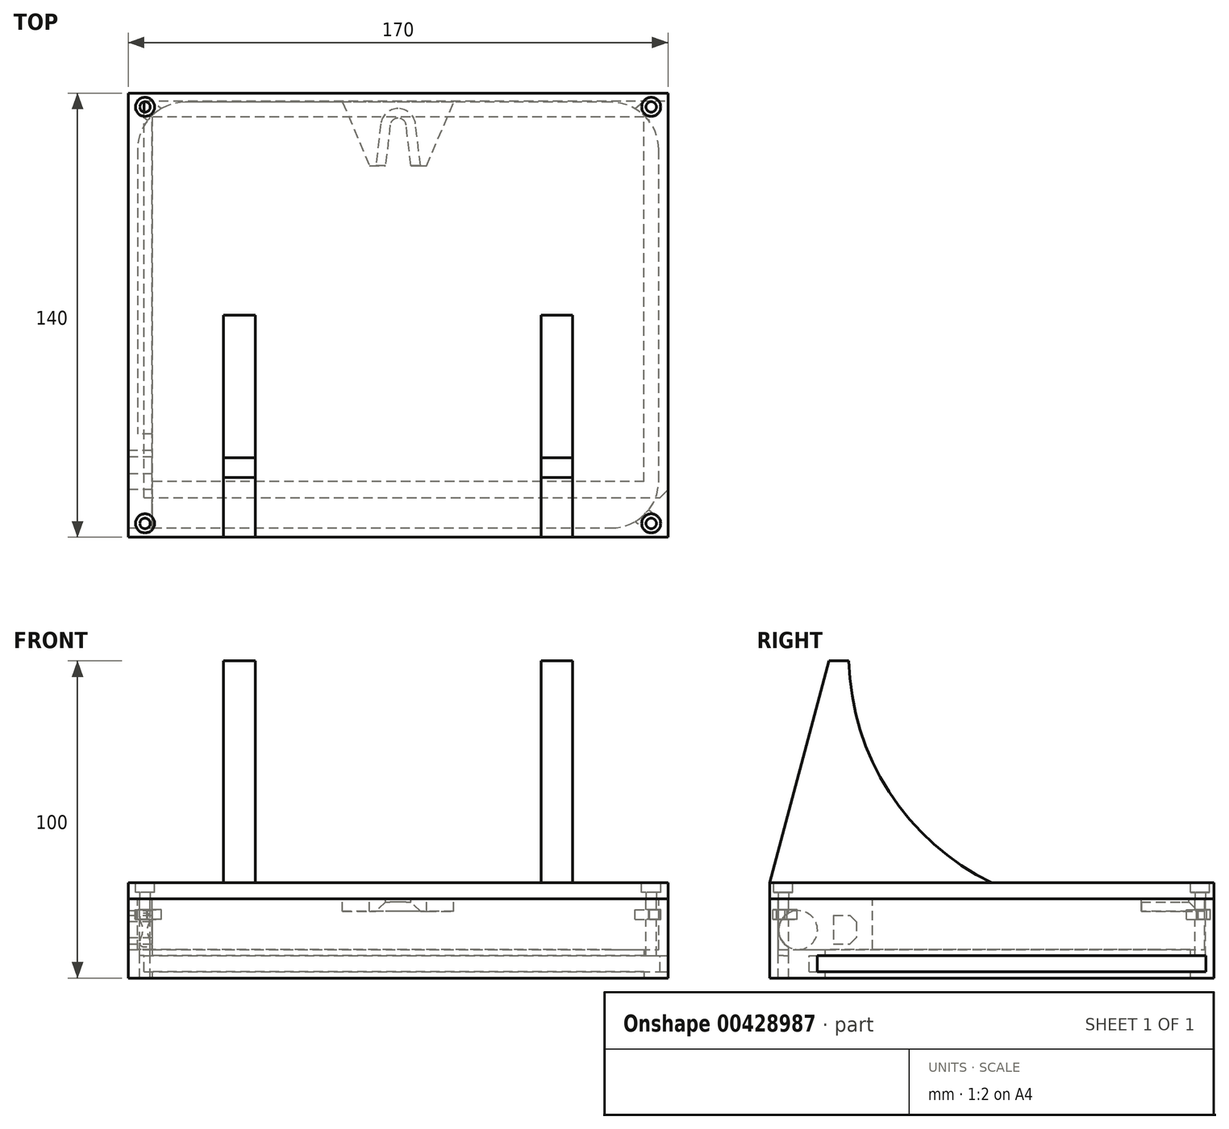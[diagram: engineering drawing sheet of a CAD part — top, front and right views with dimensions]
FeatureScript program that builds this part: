
annotation { "Feature Type Name" : "Feature", "Feature Type Description" : "" }
export const myFeature = defineFeature(function(context is Context, id is Id, definition is map)
    precondition{}
    {
        {
            var Q0;
            Q0=qCreatedBy(makeId("Top.planeOp"),FACE);
            var sketch = newSketch(context, id + "F0", { "sketchPlane" : qUnion([Q0])});
            skLineSegment(sketch, "E0.bottom", {"start": v(0, 0) * mm, "end": v(170, 0) * mm});
            skLineSegment(sketch, "E0.top", {"start": v(0, 140) * mm, "end": v(170, 140) * mm});
            skLineSegment(sketch, "E0.left", {"start": v(0, 0) * mm, "end": v(0, 140) * mm});
            skLineSegment(sketch, "E0.right", {"start": v(170, 0) * mm, "end": v(170, 140) * mm});
            skLineSegment(sketch, "E1.bottom", {"start": v(7.5, 132.5) * mm, "end": v(162.5, 132.5) * mm});
            skLineSegment(sketch, "E1.top", {"start": v(7.5, 17.5) * mm, "end": v(162.5, 17.5) * mm});
            skLineSegment(sketch, "E1.left", {"start": v(7.5, 132.5) * mm, "end": v(7.5, 17.5) * mm});
            skLineSegment(sketch, "E1.right", {"start": v(162.5, 132.5) * mm, "end": v(162.5, 17.5) * mm});
            skSolve(sketch);
        }
        {
            var Q0;
            Q0=qSketchRegion(id+"F0",true);
            extrude(context, id + "F1", {"entities" : qUnion([Q0]), "depth" : 25 * mm});
        }
        {
            var Q0;
            Q0=makeQuery(id+"F1.opExtrude","SWEPT_FACE",FACE,{"disambiguationData":[OSD([sQuery(id+"F0.wireOp",EDGE,"E0.right")])]});
            var sketch = newSketch(context, id + "F2", { "sketchPlane" : qUnion([Q0])});
            skLineSegment(sketch, "E2.0.0", {"start": v(17.5, 0) * mm, "end": v(132.5, 0) * mm, "construction": true});
            skLineSegment(sketch, "E2.0.1", {"start": v(132.5, 0) * mm, "end": v(132.5, 25) * mm, "construction": true});
            skLineSegment(sketch, "E2.0.2", {"start": v(132.5, 25) * mm, "end": v(17.5, 25) * mm, "construction": true});
            skLineSegment(sketch, "E2.0.3", {"start": v(17.5, 25) * mm, "end": v(17.5, 0) * mm, "construction": true});
            skLineSegment(sketch, "E3.0.3", {"start": v(132.5, 25) * mm, "end": v(132.5, 0) * mm, "construction": true});
            skLineSegment(sketch, "E4.bottom", {"start": v(12.5, 2) * mm, "end": v(137.5, 2) * mm});
            skLineSegment(sketch, "E4.top", {"start": v(12.5, 7) * mm, "end": v(137.5, 7) * mm});
            skLineSegment(sketch, "E4.left", {"start": v(12.5, 2) * mm, "end": v(12.5, 7) * mm});
            skLineSegment(sketch, "E4.right", {"start": v(137.5, 2) * mm, "end": v(137.5, 7) * mm});
            skSolve(sketch);
        }
        {
            var Q0;
            Q0=qSketchRegion(id+"F2",true);
            extrude(context, id + "F3", {"entities" : qUnion([Q0]), "operationType" : NewBodyOperationType.REMOVE, "oppositeDirection" : true, "depth" : 165 * mm});
        }
        {
            var Q0;
            Q0=makeQuery(id+"F3.boolean.opBoolean","COPY",FACE,{"derivedFrom":makeQuery(id+"F3.opExtrude","SWEPT_FACE",FACE,{"disambiguationData":[OSD([sQuery(id+"F2.wireOp",EDGE,"E4.top")])]})});
            var sketch = newSketch(context, id + "F4", { "sketchPlane" : qUnion([Q0])});
            skLineSegment(sketch, "E5", {"start": v(167.5, -12.5) * mm, "end": v(170, -15) * mm});
            skLineSegment(sketch, "E6", {"start": v(170, -15) * mm, "end": v(170, -12.5) * mm});
            skLineSegment(sketch, "E7", {"start": v(170, -12.5) * mm, "end": v(167.5, -12.5) * mm});
            skSolve(sketch);
        }
        {
            var Q0;
            Q0=makeQuery(id+"F4.imprint","IMPRINT",FACE,{"disambiguationData":[TD([[makeQuery(id+"F4.imprint","IMPRINT",EDGE,{"derivedFrom":sQuery(id+"F4.wireOp",EDGE,"E5")}),1.0]])]});
            extrude(context, id + "F5", {"entities" : qUnion([Q0]), "operationType" : NewBodyOperationType.ADD, "endBound" : BoundingType.UP_TO_NEXT, "depth" : 25 * mm});
        }
        {
            var Q0;
            Q0=makeQuery(id+"F1.opExtrude","CAP_FACE",FACE,{"disambiguationData":[OSD([sQuery(id+"F0.wireOp",EDGE,"E0.bottom"),sQuery(id+"F0.wireOp",EDGE,"E0.top"),sQuery(id+"F0.wireOp",EDGE,"E0.left"),sQuery(id+"F0.wireOp",EDGE,"E0.right"),sQuery(id+"F0.wireOp",EDGE,"E1.bottom"),sQuery(id+"F0.wireOp",EDGE,"E1.top"),sQuery(id+"F0.wireOp",EDGE,"E1.left"),sQuery(id+"F0.wireOp",EDGE,"E1.right")])],"isStart":false});
            var sketch = newSketch(context, id + "F6", { "sketchPlane" : qUnion([Q0])});
            skLineSegment(sketch, "E8.0", {"start": v(167.12, 137.12) * mm, "end": v(2.88, 137.12) * mm});
            skLineSegment(sketch, "E8.1", {"start": v(167.12, 2.88) * mm, "end": v(167.12, 137.12) * mm});
            skLineSegment(sketch, "E8.2", {"start": v(2.88, 2.88) * mm, "end": v(167.12, 2.88) * mm});
            skLineSegment(sketch, "E8.3", {"start": v(2.88, 137.12) * mm, "end": v(2.88, 2.88) * mm});
            skSolve(sketch);
        }
        {
            var Q0;
            Q0=qSketchRegion(id+"F6",true);
            extrude(context, id + "F7", {"entities" : qUnion([Q0]), "operationType" : NewBodyOperationType.REMOVE, "oppositeDirection" : true, "depth" : 16 * mm});
        }
        {
            var Q0;
            Q0=makeQuery(id+"F7.boolean.opBoolean","COPY",EDGE,{"derivedFrom":makeQuery(id+"F7.opExtrude","SWEPT_EDGE",EDGE,{"disambiguationData":[OSD([sQuery(id+"F6.wireOp",EDGE,"E8.0"),sQuery(id+"F6.wireOp",EDGE,"E8.3")])]})});
            var Q1;
            Q1=makeQuery(id+"F7.boolean.opBoolean","COPY",EDGE,{"derivedFrom":makeQuery(id+"F7.opExtrude","SWEPT_EDGE",EDGE,{"disambiguationData":[OSD([sQuery(id+"F6.wireOp",EDGE,"E8.0"),sQuery(id+"F6.wireOp",EDGE,"E8.1")])]})});
            var Q2;
            Q2=makeQuery(id+"F7.boolean.opBoolean","COPY",EDGE,{"derivedFrom":makeQuery(id+"F7.opExtrude","SWEPT_EDGE",EDGE,{"disambiguationData":[OSD([sQuery(id+"F6.wireOp",EDGE,"E8.1"),sQuery(id+"F6.wireOp",EDGE,"E8.2")])]})});
            fillet(context, id + "F8", {"entities" : qUnion([Q0, Q1, Q2]), "radius" : 15 * mm, "tangentPropagation" : true, "allowEdgeOverflow" : false});
        }
        {
            var Q0;
            Q0=makeQuery(id+"F7.boolean.opBoolean","COPY",FACE,{"derivedFrom":makeQuery(id+"F7.opExtrude","SWEPT_FACE",FACE,{"disambiguationData":[OSD([sQuery(id+"F6.wireOp",EDGE,"E8.3")])]})});
            var sketch = newSketch(context, id + "F9", { "sketchPlane" : qUnion([Q0])});
            skLineSegment(sketch, "E9.0.0", {"start": v(2.88, 9) * mm, "end": v(122.12, 9) * mm, "construction": true});
            skLineSegment(sketch, "E9.0.1", {"start": v(122.12, 9) * mm, "end": v(122.12, 25) * mm, "construction": true});
            skLineSegment(sketch, "E9.0.2", {"start": v(122.12, 25) * mm, "end": v(2.88, 25) * mm, "construction": true});
            skLineSegment(sketch, "E9.0.3", {"start": v(2.88, 25) * mm, "end": v(2.88, 9) * mm, "construction": true});
            skCircle(sketch, "E10", {"center": v(9, 15.13) * mm, "radius": 6.12 * mm});
            skSolve(sketch);
        }
        {
            var Q0;
            {var subQ0=sQuery(id+"F9.wireOp",EDGE,"E10");var subQ1=sQuery(id+"F6.wireOp",EDGE,"E8.3");var subQ3=makeQuery(id+"F9.imprint","INTERSECT",VERTEX,{"derivedFrom":[makeQuery(id+"F7.boolean.opBoolean","COPY",EDGE,{"derivedFrom":makeQuery(id+"F7.opExtrude","CAP_EDGE",EDGE,{"disambiguationData":[OSD([subQ1])],"isStart":false})}),subQ0]});Q0=makeQuery(id+"F9.imprint","IMPRINT",FACE,{"disambiguationData":[TD([[makeQuery(id+"F9.imprint","IMPRINT",EDGE,{"disambiguationData":[TD([[subQ3,1.0]])],"derivedFrom":subQ0}),1.0]])]});}
            extrude(context, id + "F10", {"entities" : qUnion([Q0]), "operationType" : NewBodyOperationType.REMOVE, "endBound" : BoundingType.THROUGH_ALL, "oppositeDirection" : true, "depth" : 25 * mm});
        }
        {
            var Q0;
            {var subQ0=sQuery(id+"F6.wireOp",EDGE,"E8.3");var subQ1=makeQuery(id+"F7.boolean.opBoolean","COPY",FACE,{"derivedFrom":makeQuery(id+"F7.opExtrude","SWEPT_FACE",FACE,{"disambiguationData":[OSD([subQ0])]})});var subQ2=sQuery(id+"F6.wireOp",EDGE,"E8.2");var subQ3=sQuery(id+"F6.wireOp",EDGE,"E8.0");Q0=makeQuery(id+"F10.boolean.opBoolean","SPLIT",FACE,{"disambiguationData":[TD([makeQuery(id+"F1.opExtrude","CAP_FACE",FACE,{"disambiguationData":[OSD([sQuery(id+"F0.wireOp",EDGE,"E0.bottom"),sQuery(id+"F0.wireOp",EDGE,"E0.top"),sQuery(id+"F0.wireOp",EDGE,"E0.left"),sQuery(id+"F0.wireOp",EDGE,"E0.right"),sQuery(id+"F0.wireOp",EDGE,"E1.bottom"),sQuery(id+"F0.wireOp",EDGE,"E1.top"),sQuery(id+"F0.wireOp",EDGE,"E1.left"),sQuery(id+"F0.wireOp",EDGE,"E1.right")])],"isStart":false}),makeQuery(id+"F7.boolean.opBoolean","COPY",FACE,{"derivedFrom":makeQuery(id+"F7.opExtrude","CAP_FACE",FACE,{"disambiguationData":[OSD([subQ3,sQuery(id+"F6.wireOp",EDGE,"E8.1"),subQ2,subQ0])],"isStart":false})}),makeQuery(id+"F7.boolean.opBoolean","COPY",FACE,{"derivedFrom":makeQuery(id+"F7.opExtrude","SWEPT_FACE",FACE,{"disambiguationData":[OSD([subQ2])]})}),subQ1,makeQuery(id+"F8.opFillet","BLEND_FACE",FACE,{"disambiguationData":[OSD([subQ3,subQ0])]}),makeQuery(id+"F10.opExtrude","SWEPT_FACE",FACE,{"disambiguationData":[OSD([sQuery(id+"F9.wireOp",EDGE,"E10")])]})])],"derivedFrom":subQ1});}
            var sketch = newSketch(context, id + "F11", { "sketchPlane" : qUnion([Q0])});
            skArc(sketch, "E11.0", {"start": v(9, 9) * mm, "mid": v(13.34, 19.46) * mm, "end": v(2.88, 15.13) * mm});
            skArc(sketch, "E12.0", {"start": v(2.88, 15.13) * mm, "mid": v(4.67, 10.8) * mm, "end": v(9, 9) * mm});
            skLineSegment(sketch, "E13.bottom", {"start": v(2.88, 9) * mm, "end": v(17.5, 9) * mm});
            skLineSegment(sketch, "E13.top", {"start": v(2.88, 25) * mm, "end": v(17.5, 25) * mm});
            skLineSegment(sketch, "E13.left", {"start": v(2.88, 9) * mm, "end": v(2.88, 25) * mm});
            skLineSegment(sketch, "E13.right", {"start": v(17.5, 9) * mm, "end": v(17.5, 9) * mm});
            skLineSegment(sketch, "E14.0", {"start": v(17.5, 9) * mm, "end": v(17.5, 7) * mm, "construction": true});
            skLineSegment(sketch, "E15", {"start": v(17.5, 9) * mm, "end": v(17.5, 25) * mm});
            skSolve(sketch);
        }
        {
            var Q0;
            Q0=qSketchRegion(id+"F11",true);
            var Q1;
            {var subQ0=sQuery(id+"F0.wireOp",EDGE,"E1.left");Q1=makeQuery(id+"F3.boolean.opBoolean","SPLIT",FACE,{"disambiguationData":[TD([makeQuery(id+"F3.opExtrude","SWEPT_FACE",FACE,{"disambiguationData":[OSD([sQuery(id+"F2.wireOp",EDGE,"E4.top")])]})])],"derivedFrom":makeQuery(id+"F1.opExtrude","SWEPT_FACE",FACE,{"disambiguationData":[OSD([subQ0])]})});}
            extrude(context, id + "F12", {"entities" : qUnion([Q0]), "operationType" : NewBodyOperationType.ADD, "endBound" : BoundingType.UP_TO_SURFACE, "endBoundEntityFace" : qUnion([Q1]), "depth" : 7.5 * mm});
        }
        {
            var Q0;
            Q0=makeQuery(id+"F12.opExtrude","CAP_FACE",FACE,{"disambiguationData":[OSD([sQuery(id+"F11.wireOp",EDGE,"E13.bottom"),sQuery(id+"F11.wireOp",EDGE,"E13.top"),sQuery(id+"F11.wireOp",EDGE,"E13.left"),sQuery(id+"F11.wireOp",EDGE,"E15")])],"isStart":true});
            extrude(context, id + "F13", {"entities" : qUnion([Q0]), "operationType" : NewBodyOperationType.REMOVE, "endBound" : BoundingType.UP_TO_NEXT, "oppositeDirection" : true, "depth" : 25 * mm});
        }
        {
            var Q0;
            Q0=makeQuery(id+"F12.opExtrude","SWEPT_FACE",FACE,{"disambiguationData":[OSD([sQuery(id+"F11.wireOp",EDGE,"E15")])]});
            extrude(context, id + "F14", {"entities" : qUnion([Q0]), "operationType" : NewBodyOperationType.ADD, "depth" : 15 * mm});
        }
        {
            var Q0;
            {var subQ0=sQuery(id+"F11.wireOp",EDGE,"E15");var subQ1=sQuery(id+"F6.wireOp",EDGE,"E8.2");var subQ2=sQuery(id+"F11.wireOp",EDGE,"E13.top");var subQ3=makeQuery(id+"F12.opExtrude","CAP_FACE",FACE,{"disambiguationData":[OSD([sQuery(id+"F11.wireOp",EDGE,"E13.bottom"),subQ2,sQuery(id+"F11.wireOp",EDGE,"E13.left"),subQ0])],"isStart":false});var subQ4=sQuery(id+"F0.wireOp",EDGE,"E1.left");var subQ5=makeQuery(id+"F1.opExtrude","SWEPT_FACE",FACE,{"disambiguationData":[OSD([subQ4])]});var subQ6=sQuery(id+"F0.wireOp",EDGE,"E1.top");var subQ7=makeQuery(id+"F1.opExtrude","SWEPT_FACE",FACE,{"disambiguationData":[OSD([subQ6])]});var subQ8=sQuery(id+"F0.wireOp",EDGE,"E1.bottom");var subQ9=makeQuery(id+"F1.opExtrude","CAP_FACE",FACE,{"disambiguationData":[OSD([sQuery(id+"F0.wireOp",EDGE,"E0.bottom"),sQuery(id+"F0.wireOp",EDGE,"E0.top"),sQuery(id+"F0.wireOp",EDGE,"E0.left"),sQuery(id+"F0.wireOp",EDGE,"E0.right"),subQ8,subQ6,subQ4,sQuery(id+"F0.wireOp",EDGE,"E1.right")])],"isStart":false});var subQ10=sQuery(id+"F9.wireOp",EDGE,"E10");Q0=makeQuery(id+"F14.boolean.opBoolean","MERGE",FACE,{"derivedFrom":[makeQuery(id+"F3.boolean.opBoolean","SPLIT",FACE,{"disambiguationData":[TD([makeQuery(id+"F3.opExtrude","SWEPT_FACE",FACE,{"disambiguationData":[OSD([sQuery(id+"F2.wireOp",EDGE,"E4.top")])]})])],"derivedFrom":subQ5}),makeQuery(id+"F13.boolean.opBoolean","SPLIT",FACE,{"disambiguationData":[TD([subQ9,subQ7,subQ5,makeQuery(id+"F7.boolean.opBoolean","COPY",FACE,{"derivedFrom":makeQuery(id+"F7.opExtrude","CAP_FACE",FACE,{"disambiguationData":[OSD([sQuery(id+"F6.wireOp",EDGE,"E8.0"),sQuery(id+"F6.wireOp",EDGE,"E8.1"),subQ1,sQuery(id+"F6.wireOp",EDGE,"E8.3")])],"isStart":false})}),makeQuery(id+"F7.boolean.opBoolean","COPY",FACE,{"derivedFrom":makeQuery(id+"F7.opExtrude","SWEPT_FACE",FACE,{"disambiguationData":[OSD([subQ1])]})}),makeQuery(id+"F10.boolean.opBoolean","COPY",FACE,{"derivedFrom":makeQuery(id+"F10.opExtrude","SWEPT_FACE",FACE,{"disambiguationData":[OSD([subQ10])]})}),subQ3,makeQuery(id+"F12.opExtrude","SWEPT_FACE",FACE,{"disambiguationData":[OSD([subQ2])]}),makeQuery(id+"F12.opExtrude","SWEPT_FACE",FACE,{"disambiguationData":[OSD([subQ0])]}),makeQuery(id+"F13.opExtrude","SWEPT_FACE",FACE,{"disambiguationData":[OSD([subQ10])]})])],"derivedFrom":subQ3}),makeQuery(id+"F14.opExtrude","SWEPT_FACE",FACE,{"disambiguationData":[OSD([subQ0]),TDD([makeQuery(id+"F12.opExtrude","CAP_EDGE",EDGE,{"disambiguationData":[OSD([subQ0])],"isStart":false})])]})]});}
            var sketch = newSketch(context, id + "F15", { "sketchPlane" : qUnion([Q0])});
            skLineSegment(sketch, "E16.bottom", {"start": v(20.13, 19.75) * mm, "end": v(27.38, 19.75) * mm});
            skLineSegment(sketch, "E16.top", {"start": v(20.13, 10.75) * mm, "end": v(27.38, 10.75) * mm});
            skLineSegment(sketch, "E16.left", {"start": v(20.13, 19.75) * mm, "end": v(20.13, 10.75) * mm});
            skLineSegment(sketch, "E16.right", {"start": v(27.38, 19.75) * mm, "end": v(27.38, 10.75) * mm});
            skLineSegment(sketch, "E17.0", {"start": v(9, 9) * mm, "end": v(17.5, 9) * mm, "construction": true});
            skSolve(sketch);
        }
        {
            var Q0;
            Q0=makeQuery(id+"F15.imprint","IMPRINT",FACE,{"disambiguationData":[TD([[makeQuery(id+"F15.imprint","IMPRINT",EDGE,{"derivedFrom":sQuery(id+"F15.wireOp",EDGE,"E16.bottom")}),-1.0]])]});
            extrude(context, id + "F16", {"entities" : qUnion([Q0]), "operationType" : NewBodyOperationType.REMOVE, "endBound" : BoundingType.UP_TO_NEXT, "oppositeDirection" : true, "depth" : 25 * mm});
        }
        {
            var Q0;
            Q0=makeQuery(id+"F16.boolean.opBoolean","COPY",EDGE,{"derivedFrom":makeQuery(id+"F16.opExtrude","SWEPT_EDGE",EDGE,{"disambiguationData":[OSD([sQuery(id+"F15.wireOp",EDGE,"E16.top"),sQuery(id+"F15.wireOp",EDGE,"E16.right")])]})});
            var Q1;
            Q1=makeQuery(id+"F16.boolean.opBoolean","COPY",EDGE,{"derivedFrom":makeQuery(id+"F16.opExtrude","SWEPT_EDGE",EDGE,{"disambiguationData":[OSD([sQuery(id+"F15.wireOp",EDGE,"E16.bottom"),sQuery(id+"F15.wireOp",EDGE,"E16.right")])]})});
            chamfer(context, id + "F17", {"entities" : qUnion([Q0, Q1]), "width" : 2 * mm, "tangentPropagation" : true});
        }
        {
            var Q0;
            {var subQ0=sQuery(id+"F11.wireOp",EDGE,"E13.top");Q0=makeQuery(id+"F14.boolean.opBoolean","MERGE",FACE,{"derivedFrom":[makeQuery(id+"F12.boolean.opBoolean","MERGE",FACE,{"derivedFrom":[makeQuery(id+"F1.opExtrude","CAP_FACE",FACE,{"disambiguationData":[OSD([sQuery(id+"F0.wireOp",EDGE,"E0.bottom"),sQuery(id+"F0.wireOp",EDGE,"E0.top"),sQuery(id+"F0.wireOp",EDGE,"E0.left"),sQuery(id+"F0.wireOp",EDGE,"E0.right"),sQuery(id+"F0.wireOp",EDGE,"E1.bottom"),sQuery(id+"F0.wireOp",EDGE,"E1.top"),sQuery(id+"F0.wireOp",EDGE,"E1.left"),sQuery(id+"F0.wireOp",EDGE,"E1.right")])],"isStart":false}),makeQuery(id+"F12.opExtrude","SWEPT_FACE",FACE,{"disambiguationData":[OSD([subQ0])]})]}),makeQuery(id+"F14.opExtrude","SWEPT_FACE",FACE,{"disambiguationData":[OSD([sQuery(id+"F6.wireOp",EDGE,"E8.3"),subQ0,sQuery(id+"F11.wireOp",EDGE,"E15")])]})]});}
            var sketch = newSketch(context, id + "F18", { "sketchPlane" : qUnion([Q0])});
            skLineSegment(sketch, "E18", {"start": v(67.5, 137.12) * mm, "end": v(76, 117.12) * mm});
            skLineSegment(sketch, "E19", {"start": v(76, 117.12) * mm, "end": v(81, 117.12) * mm});
            skLineSegment(sketch, "E20", {"start": v(89, 117.12) * mm, "end": v(87.25, 132.12) * mm});
            skLineSegment(sketch, "E21", {"start": v(82.75, 132.12) * mm, "end": v(87.25, 132.12) * mm});
            skLineSegment(sketch, "E22", {"start": v(82.75, 132.12) * mm, "end": v(81, 117.12) * mm});
            skLineSegment(sketch, "E23", {"start": v(89, 117.12) * mm, "end": v(94, 117.12) * mm});
            skLineSegment(sketch, "E24", {"start": v(94, 117.12) * mm, "end": v(102.5, 137.12) * mm});
            skLineSegment(sketch, "E25", {"start": v(102.5, 137.12) * mm, "end": v(67.5, 137.12) * mm});
            skSolve(sketch);
        }
        {
            var Q0;
            Q0=qSketchRegion(id+"F18",true);
            extrude(context, id + "F19", {"entities" : qUnion([Q0]), "operationType" : NewBodyOperationType.ADD, "oppositeDirection" : true, "depth" : 4 * mm});
        }
        {
            var Q0;
            Q0=makeQuery(id+"F19.opExtrude","SWEPT_EDGE",EDGE,{"disambiguationData":[OSD([sQuery(id+"F18.wireOp",EDGE,"E21"),sQuery(id+"F18.wireOp",EDGE,"E22")])]});
            var Q1;
            Q1=makeQuery(id+"F19.opExtrude","SWEPT_EDGE",EDGE,{"disambiguationData":[OSD([sQuery(id+"F18.wireOp",EDGE,"E20"),sQuery(id+"F18.wireOp",EDGE,"E21")])]});
            fillet(context, id + "F20", {"entities" : qUnion([Q0, Q1]), "radius" : 2.5 * mm, "tangentPropagation" : true, "allowEdgeOverflow" : false});
        }
        {
            var Q0;
            {var subQ0=sQuery(id+"F18.wireOp",EDGE,"E22");var subQ1=sQuery(id+"F18.wireOp",EDGE,"E21");Q0=makeQuery(id+"F20.opFillet","BLEND_EDGE",EDGE,{"blendedFrom":[makeQuery(id+"F19.opExtrude","SWEPT_EDGE",EDGE,{"disambiguationData":[OSD([subQ1,subQ0])]}),makeQuery(id+"F19.opExtrude","CAP_FACE",FACE,{"disambiguationData":[OSD([sQuery(id+"F18.wireOp",EDGE,"E18"),sQuery(id+"F18.wireOp",EDGE,"E19"),sQuery(id+"F18.wireOp",EDGE,"E20"),subQ1,subQ0,sQuery(id+"F18.wireOp",EDGE,"E23"),sQuery(id+"F18.wireOp",EDGE,"E24"),sQuery(id+"F18.wireOp",EDGE,"E25")])],"isStart":false})],"blendedInto":[makeQuery(id+"F19.opExtrude","CAP_FACE",FACE,{"disambiguationData":[OSD([sQuery(id+"F18.wireOp",EDGE,"E18"),sQuery(id+"F18.wireOp",EDGE,"E19"),sQuery(id+"F18.wireOp",EDGE,"E20"),subQ1,subQ0,sQuery(id+"F18.wireOp",EDGE,"E23"),sQuery(id+"F18.wireOp",EDGE,"E24"),sQuery(id+"F18.wireOp",EDGE,"E25")])],"isStart":false})]});}
            chamfer(context, id + "F21", {"entities" : qUnion([Q0]), "width" : 3 * mm, "tangentPropagation" : true});
        }
        {
            var Q0;
            {var subQ0=sQuery(id+"F11.wireOp",EDGE,"E13.top");Q0=makeQuery(id+"F19.boolean.opBoolean","MERGE",FACE,{"derivedFrom":[makeQuery(id+"F14.boolean.opBoolean","MERGE",FACE,{"derivedFrom":[makeQuery(id+"F12.boolean.opBoolean","MERGE",FACE,{"derivedFrom":[makeQuery(id+"F1.opExtrude","CAP_FACE",FACE,{"disambiguationData":[OSD([sQuery(id+"F0.wireOp",EDGE,"E0.bottom"),sQuery(id+"F0.wireOp",EDGE,"E0.top"),sQuery(id+"F0.wireOp",EDGE,"E0.left"),sQuery(id+"F0.wireOp",EDGE,"E0.right"),sQuery(id+"F0.wireOp",EDGE,"E1.bottom"),sQuery(id+"F0.wireOp",EDGE,"E1.top"),sQuery(id+"F0.wireOp",EDGE,"E1.left"),sQuery(id+"F0.wireOp",EDGE,"E1.right")])],"isStart":false}),makeQuery(id+"F12.opExtrude","SWEPT_FACE",FACE,{"disambiguationData":[OSD([subQ0])]})]}),makeQuery(id+"F14.opExtrude","SWEPT_FACE",FACE,{"disambiguationData":[OSD([sQuery(id+"F6.wireOp",EDGE,"E8.3"),subQ0,sQuery(id+"F11.wireOp",EDGE,"E15")])]})]}),makeQuery(id+"F19.opExtrude","CAP_FACE",FACE,{"disambiguationData":[OSD([sQuery(id+"F18.wireOp",EDGE,"E18"),sQuery(id+"F18.wireOp",EDGE,"E19"),sQuery(id+"F18.wireOp",EDGE,"E20"),sQuery(id+"F18.wireOp",EDGE,"E21"),sQuery(id+"F18.wireOp",EDGE,"E22"),sQuery(id+"F18.wireOp",EDGE,"E23"),sQuery(id+"F18.wireOp",EDGE,"E24"),sQuery(id+"F18.wireOp",EDGE,"E25")])],"isStart":true})]});}
            cPlane(context, id + "F22", {"entities" : qUnion([Q0]), "cplaneType" : CPlaneType.OFFSET, "offset" : 5 * mm, "oppositeDirection" : true, "width" : 150 * mm, "height" : 150 * mm});
        }
        {
            var Q0;
            Q0=qCreatedBy(id+"F22.planeOp",FACE);
            var sketch = newSketch(context, id + "F23", { "sketchPlane" : qUnion([Q0])});
            skLineSegment(sketch, "E26.0.0", {"start": v(170, 140) * mm, "end": v(0, 140) * mm, "construction": true});
            skLineSegment(sketch, "E26.0.1", {"start": v(0, 140) * mm, "end": v(0, 0) * mm, "construction": true});
            skLineSegment(sketch, "E26.0.2", {"start": v(0, 0) * mm, "end": v(170, 0) * mm, "construction": true});
            skLineSegment(sketch, "E26.0.3", {"start": v(170, 0) * mm, "end": v(170, 140) * mm, "construction": true});
            skLineSegment(sketch, "E27", {"start": v(0, 140) * mm, "end": v(170, 0) * mm, "construction": true});
            skLineSegment(sketch, "E28", {"start": v(0, 0) * mm, "end": v(170, 140) * mm, "construction": true});
            skCircle(sketch, "E29.cCircle", {"center": v(5.27, 135.66) * mm, "radius": 2.85 * mm, "construction": true});
            skLineSegment(sketch, "E29.0", {"start": v(5.81, 138.9) * mm, "end": v(8.35, 136.81) * mm});
            skLineSegment(sketch, "E29.1", {"start": v(8.35, 136.81) * mm, "end": v(7.81, 133.57) * mm, "construction": true});
            skLineSegment(sketch, "E29.2", {"start": v(7.81, 133.57) * mm, "end": v(4.73, 132.41) * mm, "construction": true});
            skLineSegment(sketch, "E29.3", {"start": v(4.73, 132.41) * mm, "end": v(2.2, 134.5) * mm});
            skLineSegment(sketch, "E29.4", {"start": v(2.2, 134.5) * mm, "end": v(2.73, 137.75) * mm});
            skLineSegment(sketch, "E29.5", {"start": v(2.73, 137.75) * mm, "end": v(5.81, 138.9) * mm});
            skPoint(sketch, "E29.0.midPoint", {"position": v(7.08, 137.86) * mm});
            skCircle(sketch, "E30.cCircle", {"center": v(164.73, 135.66) * mm, "radius": 2.85 * mm, "construction": true});
            skLineSegment(sketch, "E30.0", {"start": v(161.65, 136.81) * mm, "end": v(164.19, 138.9) * mm});
            skLineSegment(sketch, "E30.1", {"start": v(164.19, 138.9) * mm, "end": v(167.27, 137.75) * mm});
            skLineSegment(sketch, "E30.2", {"start": v(167.27, 137.75) * mm, "end": v(167.8, 134.5) * mm});
            skLineSegment(sketch, "E30.3", {"start": v(167.8, 134.5) * mm, "end": v(165.27, 132.41) * mm});
            skLineSegment(sketch, "E30.4", {"start": v(165.27, 132.41) * mm, "end": v(162.19, 133.57) * mm, "construction": true});
            skLineSegment(sketch, "E30.5", {"start": v(162.19, 133.57) * mm, "end": v(161.65, 136.81) * mm, "construction": true});
            skPoint(sketch, "E30.0.midPoint", {"position": v(162.92, 137.86) * mm});
            skCircle(sketch, "E31.cCircle", {"center": v(164.73, 4.34) * mm, "radius": 2.85 * mm, "construction": true});
            skLineSegment(sketch, "E31.0", {"start": v(165.27, 7.59) * mm, "end": v(167.8, 5.5) * mm});
            skLineSegment(sketch, "E31.1", {"start": v(167.8, 5.5) * mm, "end": v(167.27, 2.25) * mm});
            skLineSegment(sketch, "E31.2", {"start": v(167.27, 2.25) * mm, "end": v(164.19, 1.1) * mm});
            skLineSegment(sketch, "E31.3", {"start": v(164.19, 1.1) * mm, "end": v(161.65, 3.19) * mm});
            skLineSegment(sketch, "E31.4", {"start": v(161.65, 3.19) * mm, "end": v(162.19, 6.43) * mm, "construction": true});
            skLineSegment(sketch, "E31.5", {"start": v(162.19, 6.43) * mm, "end": v(165.27, 7.59) * mm, "construction": true});
            skPoint(sketch, "E31.0.midPoint", {"position": v(166.54, 6.54) * mm});
            skArc(sketch, "E32.0", {"start": v(6.04, 131.33) * mm, "mid": v(8.04, 133.44) * mm, "end": v(10.4, 135.12) * mm});
            skArc(sketch, "E33.0", {"start": v(159.6, 135.12) * mm, "mid": v(161.96, 133.44) * mm, "end": v(163.96, 131.33) * mm});
            skArc(sketch, "E34.0", {"start": v(163.96, 8.67) * mm, "mid": v(161.96, 6.56) * mm, "end": v(159.6, 4.88) * mm});
            skLineSegment(sketch, "E35", {"start": v(4.73, 132.41) * mm, "end": v(6.04, 131.33) * mm});
            skLineSegment(sketch, "E36", {"start": v(8.35, 136.81) * mm, "end": v(10.4, 135.12) * mm});
            skLineSegment(sketch, "E37", {"start": v(165.27, 132.41) * mm, "end": v(163.96, 131.33) * mm});
            skLineSegment(sketch, "E38", {"start": v(161.65, 136.81) * mm, "end": v(159.6, 135.12) * mm});
            skLineSegment(sketch, "E39", {"start": v(165.27, 7.59) * mm, "end": v(163.96, 8.67) * mm});
            skLineSegment(sketch, "E40", {"start": v(161.65, 3.19) * mm, "end": v(159.6, 4.88) * mm});
            skPoint(sketch, "E41.orphan", {"position": v(152.12, 2.88) * mm});
            skPoint(sketch, "E42.orphan", {"position": v(167.12, 17.88) * mm});
            skPoint(sketch, "E43.orphan", {"position": v(167.12, 122.12) * mm});
            skPoint(sketch, "E44.orphan", {"position": v(152.12, 137.12) * mm});
            skPoint(sketch, "E45.orphan", {"position": v(17.88, 137.12) * mm});
            skPoint(sketch, "E46.orphan", {"position": v(2.88, 122.12) * mm});
            skSolve(sketch);
        }
        {
            var Q0;
            Q0=qSketchRegion(id+"F23",true);
            extrude(context, id + "F24", {"entities" : qUnion([Q0]), "operationType" : NewBodyOperationType.REMOVE, "endBound" : BoundingType.SYMMETRIC, "oppositeDirection" : true, "depth" : 3 * mm});
        }
        {
            var Q0;
            {var subQ0=sQuery(id+"F11.wireOp",EDGE,"E13.top");Q0=makeQuery(id+"F19.boolean.opBoolean","MERGE",FACE,{"derivedFrom":[makeQuery(id+"F14.boolean.opBoolean","MERGE",FACE,{"derivedFrom":[makeQuery(id+"F12.boolean.opBoolean","MERGE",FACE,{"derivedFrom":[makeQuery(id+"F1.opExtrude","CAP_FACE",FACE,{"disambiguationData":[OSD([sQuery(id+"F0.wireOp",EDGE,"E0.bottom"),sQuery(id+"F0.wireOp",EDGE,"E0.top"),sQuery(id+"F0.wireOp",EDGE,"E0.left"),sQuery(id+"F0.wireOp",EDGE,"E0.right"),sQuery(id+"F0.wireOp",EDGE,"E1.bottom"),sQuery(id+"F0.wireOp",EDGE,"E1.top"),sQuery(id+"F0.wireOp",EDGE,"E1.left"),sQuery(id+"F0.wireOp",EDGE,"E1.right")])],"isStart":false}),makeQuery(id+"F12.opExtrude","SWEPT_FACE",FACE,{"disambiguationData":[OSD([subQ0])]})]}),makeQuery(id+"F14.opExtrude","SWEPT_FACE",FACE,{"disambiguationData":[OSD([sQuery(id+"F6.wireOp",EDGE,"E8.3"),subQ0,sQuery(id+"F11.wireOp",EDGE,"E15")])]})]}),makeQuery(id+"F19.opExtrude","CAP_FACE",FACE,{"disambiguationData":[OSD([sQuery(id+"F18.wireOp",EDGE,"E18"),sQuery(id+"F18.wireOp",EDGE,"E19"),sQuery(id+"F18.wireOp",EDGE,"E20"),sQuery(id+"F18.wireOp",EDGE,"E21"),sQuery(id+"F18.wireOp",EDGE,"E22"),sQuery(id+"F18.wireOp",EDGE,"E23"),sQuery(id+"F18.wireOp",EDGE,"E24"),sQuery(id+"F18.wireOp",EDGE,"E25")])],"isStart":true})]});}
            var sketch = newSketch(context, id + "F25", { "sketchPlane" : qUnion([Q0])});
            skLineSegment(sketch, "E47.0.0", {"start": v(2.2, 134.5) * mm, "end": v(6.04, 131.33) * mm, "construction": true});
            skArc(sketch, "E47.0.1", {"start": v(6.04, 131.33) * mm, "mid": v(8.04, 133.44) * mm, "end": v(10.4, 135.12) * mm, "construction": true});
            skLineSegment(sketch, "E47.0.2", {"start": v(10.4, 135.12) * mm, "end": v(5.81, 138.9) * mm, "construction": true});
            skLineSegment(sketch, "E47.0.3", {"start": v(5.81, 138.9) * mm, "end": v(2.73, 137.75) * mm, "construction": true});
            skLineSegment(sketch, "E47.0.4", {"start": v(2.73, 137.75) * mm, "end": v(2.2, 134.5) * mm, "construction": true});
            skLineSegment(sketch, "E48.0.0", {"start": v(164.19, 138.9) * mm, "end": v(159.6, 135.12) * mm, "construction": true});
            skArc(sketch, "E48.0.1", {"start": v(159.6, 135.12) * mm, "mid": v(161.96, 133.44) * mm, "end": v(163.96, 131.33) * mm, "construction": true});
            skLineSegment(sketch, "E48.0.2", {"start": v(163.96, 131.33) * mm, "end": v(167.8, 134.5) * mm, "construction": true});
            skLineSegment(sketch, "E48.0.3", {"start": v(167.8, 134.5) * mm, "end": v(167.27, 137.75) * mm, "construction": true});
            skLineSegment(sketch, "E48.0.4", {"start": v(167.27, 137.75) * mm, "end": v(164.19, 138.9) * mm, "construction": true});
            skLineSegment(sketch, "E49.0.0", {"start": v(167.8, 5.5) * mm, "end": v(163.96, 8.67) * mm, "construction": true});
            skArc(sketch, "E49.0.1", {"start": v(163.96, 8.67) * mm, "mid": v(161.96, 6.56) * mm, "end": v(159.6, 4.88) * mm, "construction": true});
            skLineSegment(sketch, "E49.0.2", {"start": v(159.6, 4.88) * mm, "end": v(164.19, 1.1) * mm, "construction": true});
            skLineSegment(sketch, "E49.0.3", {"start": v(164.19, 1.1) * mm, "end": v(167.27, 2.25) * mm, "construction": true});
            skLineSegment(sketch, "E49.0.4", {"start": v(167.27, 2.25) * mm, "end": v(167.8, 5.5) * mm, "construction": true});
            skLineSegment(sketch, "E50", {"start": v(2.46, 136.13) * mm, "end": v(5.27, 135.66) * mm, "construction": true});
            skLineSegment(sketch, "E51", {"start": v(4.27, 138.33) * mm, "end": v(5.27, 135.66) * mm, "construction": true});
            skCircle(sketch, "E52", {"center": v(5.27, 135.66) * mm, "radius": 1.65 * mm});
            skLineSegment(sketch, "E53", {"start": v(165.73, 138.33) * mm, "end": v(164.73, 135.66) * mm, "construction": true});
            skLineSegment(sketch, "E54", {"start": v(167.54, 136.13) * mm, "end": v(164.73, 135.66) * mm, "construction": true});
            skCircle(sketch, "E55", {"center": v(164.73, 135.66) * mm, "radius": 1.65 * mm});
            skLineSegment(sketch, "E56", {"start": v(165.73, 1.67) * mm, "end": v(164.73, 4.34) * mm, "construction": true});
            skLineSegment(sketch, "E57", {"start": v(164.73, 4.34) * mm, "end": v(167.54, 3.87) * mm, "construction": true});
            skCircle(sketch, "E58", {"center": v(164.73, 4.34) * mm, "radius": 1.65 * mm});
            skSolve(sketch);
        }
        {
            var Q0;
            Q0=qSketchRegion(id+"F25",true);
            var Q1;
            Q1=makeQuery(id+"F3.boolean.opBoolean","COPY",FACE,{"derivedFrom":makeQuery(id+"F3.opExtrude","SWEPT_FACE",FACE,{"disambiguationData":[OSD([sQuery(id+"F2.wireOp",EDGE,"E4.top")])]})});
            extrude(context, id + "F26", {"entities" : qUnion([Q0]), "operationType" : NewBodyOperationType.REMOVE, "endBound" : BoundingType.UP_TO_SURFACE, "oppositeDirection" : true, "endBoundEntityFace" : qUnion([Q1]), "depth" : 20 * mm});
        }
        {
            var Q0;
            {var subQ0=sQuery(id+"F11.wireOp",EDGE,"E13.top");Q0=makeQuery(id+"F19.boolean.opBoolean","MERGE",FACE,{"derivedFrom":[makeQuery(id+"F14.boolean.opBoolean","MERGE",FACE,{"derivedFrom":[makeQuery(id+"F12.boolean.opBoolean","MERGE",FACE,{"derivedFrom":[makeQuery(id+"F1.opExtrude","CAP_FACE",FACE,{"disambiguationData":[OSD([sQuery(id+"F0.wireOp",EDGE,"E0.bottom"),sQuery(id+"F0.wireOp",EDGE,"E0.top"),sQuery(id+"F0.wireOp",EDGE,"E0.left"),sQuery(id+"F0.wireOp",EDGE,"E0.right"),sQuery(id+"F0.wireOp",EDGE,"E1.bottom"),sQuery(id+"F0.wireOp",EDGE,"E1.top"),sQuery(id+"F0.wireOp",EDGE,"E1.left"),sQuery(id+"F0.wireOp",EDGE,"E1.right")])],"isStart":false}),makeQuery(id+"F12.opExtrude","SWEPT_FACE",FACE,{"disambiguationData":[OSD([subQ0])]})]}),makeQuery(id+"F14.opExtrude","SWEPT_FACE",FACE,{"disambiguationData":[OSD([sQuery(id+"F6.wireOp",EDGE,"E8.3"),subQ0,sQuery(id+"F11.wireOp",EDGE,"E15")])]})]}),makeQuery(id+"F19.opExtrude","CAP_FACE",FACE,{"disambiguationData":[OSD([sQuery(id+"F18.wireOp",EDGE,"E18"),sQuery(id+"F18.wireOp",EDGE,"E19"),sQuery(id+"F18.wireOp",EDGE,"E20"),sQuery(id+"F18.wireOp",EDGE,"E21"),sQuery(id+"F18.wireOp",EDGE,"E22"),sQuery(id+"F18.wireOp",EDGE,"E23"),sQuery(id+"F18.wireOp",EDGE,"E24"),sQuery(id+"F18.wireOp",EDGE,"E25")])],"isStart":true})]});}
            var sketch = newSketch(context, id + "F27", { "sketchPlane" : qUnion([Q0])});
            skLineSegment(sketch, "E59.0.0", {"start": v(170, 140) * mm, "end": v(0, 140) * mm});
            skLineSegment(sketch, "E59.0.1", {"start": v(0, 140) * mm, "end": v(0, 0) * mm});
            skLineSegment(sketch, "E59.0.2", {"start": v(0, 0) * mm, "end": v(170, 0) * mm});
            skLineSegment(sketch, "E59.0.3", {"start": v(170, 0) * mm, "end": v(170, 140) * mm});
            skCircle(sketch, "E60.0", {"center": v(5.27, 135.66) * mm, "radius": 1.65 * mm});
            skCircle(sketch, "E61.0", {"center": v(164.73, 135.66) * mm, "radius": 1.65 * mm});
            skCircle(sketch, "E62.0", {"center": v(164.73, 4.34) * mm, "radius": 1.65 * mm});
            skSolve(sketch);
        }
        {
            var Q0;
            {var subQ0=sQuery(id+"F11.wireOp",EDGE,"E13.top");Q0=makeQuery(id+"F19.boolean.opBoolean","MERGE",FACE,{"derivedFrom":[makeQuery(id+"F14.boolean.opBoolean","MERGE",FACE,{"derivedFrom":[makeQuery(id+"F12.boolean.opBoolean","MERGE",FACE,{"derivedFrom":[makeQuery(id+"F1.opExtrude","CAP_FACE",FACE,{"disambiguationData":[OSD([sQuery(id+"F0.wireOp",EDGE,"E0.bottom"),sQuery(id+"F0.wireOp",EDGE,"E0.top"),sQuery(id+"F0.wireOp",EDGE,"E0.left"),sQuery(id+"F0.wireOp",EDGE,"E0.right"),sQuery(id+"F0.wireOp",EDGE,"E1.bottom"),sQuery(id+"F0.wireOp",EDGE,"E1.top"),sQuery(id+"F0.wireOp",EDGE,"E1.left"),sQuery(id+"F0.wireOp",EDGE,"E1.right")])],"isStart":false}),makeQuery(id+"F12.opExtrude","SWEPT_FACE",FACE,{"disambiguationData":[OSD([subQ0])]})]}),makeQuery(id+"F14.opExtrude","SWEPT_FACE",FACE,{"disambiguationData":[OSD([sQuery(id+"F6.wireOp",EDGE,"E8.3"),subQ0,sQuery(id+"F11.wireOp",EDGE,"E15")])]})]}),makeQuery(id+"F19.opExtrude","CAP_FACE",FACE,{"disambiguationData":[OSD([sQuery(id+"F18.wireOp",EDGE,"E18"),sQuery(id+"F18.wireOp",EDGE,"E19"),sQuery(id+"F18.wireOp",EDGE,"E20"),sQuery(id+"F18.wireOp",EDGE,"E21"),sQuery(id+"F18.wireOp",EDGE,"E22"),sQuery(id+"F18.wireOp",EDGE,"E23"),sQuery(id+"F18.wireOp",EDGE,"E24"),sQuery(id+"F18.wireOp",EDGE,"E25")])],"isStart":true})]});}
            var sketch = newSketch(context, id + "F28", { "sketchPlane" : qUnion([Q0])});
            skCircle(sketch, "E63.0", {"center": v(5.27, 135.66) * mm, "radius": 1.65 * mm, "construction": true});
            skCircle(sketch, "E64.0", {"center": v(164.73, 4.34) * mm, "radius": 1.65 * mm, "construction": true});
            skCircle(sketch, "E65", {"center": v(5.27, 4.34) * mm, "radius": 1.65 * mm});
            skSolve(sketch);
        }
        {
            var Q0;
            Q0=qSketchRegion(id+"F27",true);
            extrude(context, id + "F29", {"entities" : qUnion([Q0]), "depth" : 5 * mm});
        }
        {
            var Q0;
            Q0 = qSketchRegion(id + "F28", true);
            extrude(context, id + "F30", {"entities" : qUnion([Q0]), "operationType" : NewBodyOperationType.REMOVE, "oppositeDirection" : true, "depth" : 6 * mm});
        }
        {
            var Q0;
            Q0=makeQuery(id+"F29.opExtrude","CAP_FACE",FACE,{"disambiguationData":[OSD([sQuery(id+"F27.wireOp",EDGE,"E59.0.0"),sQuery(id+"F27.wireOp",EDGE,"E59.0.1"),sQuery(id+"F27.wireOp",EDGE,"E59.0.2"),sQuery(id+"F27.wireOp",EDGE,"E59.0.3"),sQuery(id+"F27.wireOp",EDGE,"E60.0"),sQuery(id+"F27.wireOp",EDGE,"E61.0"),sQuery(id+"F27.wireOp",EDGE,"E62.0")])],"isStart":false});
            var sketch = newSketch(context, id + "F31", { "sketchPlane" : qUnion([Q0])});
            skCircle(sketch, "E66.0", {"center": v(5.27, 135.66) * mm, "radius": 1.65 * mm, "construction": true});
            skCircle(sketch, "E67.0", {"center": v(164.73, 135.66) * mm, "radius": 1.65 * mm, "construction": true});
            skCircle(sketch, "E68.0", {"center": v(164.73, 4.34) * mm, "radius": 1.65 * mm, "construction": true});
            skCircle(sketch, "E69", {"center": v(164.73, 4.34) * mm, "radius": 3 * mm});
            skCircle(sketch, "E70", {"center": v(164.73, 135.66) * mm, "radius": 3 * mm});
            skCircle(sketch, "E71", {"center": v(5.27, 135.66) * mm, "radius": 3 * mm});
            skCircle(sketch, "E72", {"center": v(5.27, 4.34) * mm, "radius": 3 * mm});
            skSolve(sketch);
        }
        {
            var Q0;
            Q0=qSketchRegion(id+"F31",true);
            extrude(context, id + "F32", {"entities" : qUnion([Q0]), "operationType" : NewBodyOperationType.REMOVE, "oppositeDirection" : true, "depth" : 3 * mm});
        }
        {
            var Q0;
            Q0=makeQuery(id+"F1.opExtrude","SWEPT_FACE",FACE,{"disambiguationData":[OSD([sQuery(id+"F0.wireOp",EDGE,"E0.bottom")])]});
            cPlane(context, id + "F33", {"entities" : qUnion([Q0]), "cplaneType" : CPlaneType.OFFSET, "offset" : 5 * mm, "oppositeDirection" : true, "width" : 150 * mm, "height" : 150 * mm});
        }
        {
            var Q0;
            Q0=makeQuery(id+"F29.opExtrude","CAP_FACE",FACE,{"disambiguationData":[OSD([sQuery(id+"F27.wireOp",EDGE,"E59.0.0"),sQuery(id+"F27.wireOp",EDGE,"E59.0.1"),sQuery(id+"F27.wireOp",EDGE,"E59.0.2"),sQuery(id+"F27.wireOp",EDGE,"E59.0.3"),sQuery(id+"F27.wireOp",EDGE,"E60.0"),sQuery(id+"F27.wireOp",EDGE,"E61.0"),sQuery(id+"F27.wireOp",EDGE,"E62.0")])],"isStart":false});
            var sketch = newSketch(context, id + "F34", { "sketchPlane" : qUnion([Q0])});
            skCircle(sketch, "E73", {"center": v(5.27, 4.34) * mm, "radius": 1.65 * mm});
            skSolve(sketch);
        }
        {
            var Q0;
            Q0 = qSketchRegion(id + "F34", true);
            extrude(context, id + "F35", {"entities" : qUnion([Q0]), "operationType" : NewBodyOperationType.REMOVE, "endBound" : BoundingType.THROUGH_ALL, "oppositeDirection" : true, "depth" : 25 * mm});
        }
        {
            var Q0;
            Q0=makeQuery(id+"F29.opExtrude","SWEPT_FACE",FACE,{"disambiguationData":[OSD([sQuery(id+"F27.wireOp",EDGE,"E59.0.2")])]});
            var sketch = newSketch(context, id + "F36", { "sketchPlane" : qUnion([Q0])});
            skLineSegment(sketch, "E74.bottom", {"start": v(30, 30) * mm, "end": v(40, 30) * mm});
            skLineSegment(sketch, "E74.top", {"start": v(30, 100) * mm, "end": v(40, 100) * mm});
            skLineSegment(sketch, "E74.left", {"start": v(30, 30) * mm, "end": v(30, 100) * mm});
            skLineSegment(sketch, "E74.right", {"start": v(40, 30) * mm, "end": v(40, 100) * mm});
            skLineSegment(sketch, "E75.bottom", {"start": v(140, 30) * mm, "end": v(130, 30) * mm});
            skLineSegment(sketch, "E75.top", {"start": v(140, 100) * mm, "end": v(130, 100) * mm});
            skLineSegment(sketch, "E75.left", {"start": v(140, 30) * mm, "end": v(140, 100) * mm});
            skLineSegment(sketch, "E75.right", {"start": v(130, 30) * mm, "end": v(130, 100) * mm});
            skSolve(sketch);
        }
        {
            var Q0;
            Q0 = qSketchRegion(id + "F36", true);
            extrude(context, id + "F37", {"entities" : qUnion([Q0]), "operationType" : NewBodyOperationType.ADD, "oppositeDirection" : true, "depth" : 70 * mm});
        }
        {
            var Q0;
            Q0=makeQuery(id+"F37.opExtrude","SWEPT_FACE",FACE,{"disambiguationData":[OSD([sQuery(id+"F36.wireOp",EDGE,"E74.left")])]});
            var sketch = newSketch(context, id + "F38", { "sketchPlane" : qUnion([Q0])});
            skArc(sketch, "E76", {"start": v(-70, 30) * mm, "mid": v(-37.68, 58.69) * mm, "end": v(-25, 100) * mm});
            skLineSegment(sketch, "E77", {"start": v(-18.76, 100) * mm, "end": v(0, 30) * mm});
            skLineSegment(sketch, "E78", {"start": v(0, 30) * mm, "end": v(0, 100) * mm});
            skLineSegment(sketch, "E79", {"start": v(0, 100) * mm, "end": v(-18.76, 100) * mm});
            skLineSegment(sketch, "E80", {"start": v(-25, 100) * mm, "end": v(-70, 100) * mm});
            skLineSegment(sketch, "E81", {"start": v(-70, 30) * mm, "end": v(-70, 100) * mm});
            skSolve(sketch);
        }
        {
            var Q0;
            Q0 = qSketchRegion(id + "F38", true);
            extrude(context, id + "F39", {"entities" : qUnion([Q0]), "operationType" : NewBodyOperationType.REMOVE, "endBound" : BoundingType.THROUGH_ALL, "oppositeDirection" : true, "depth" : 25 * mm});
        }
    });
